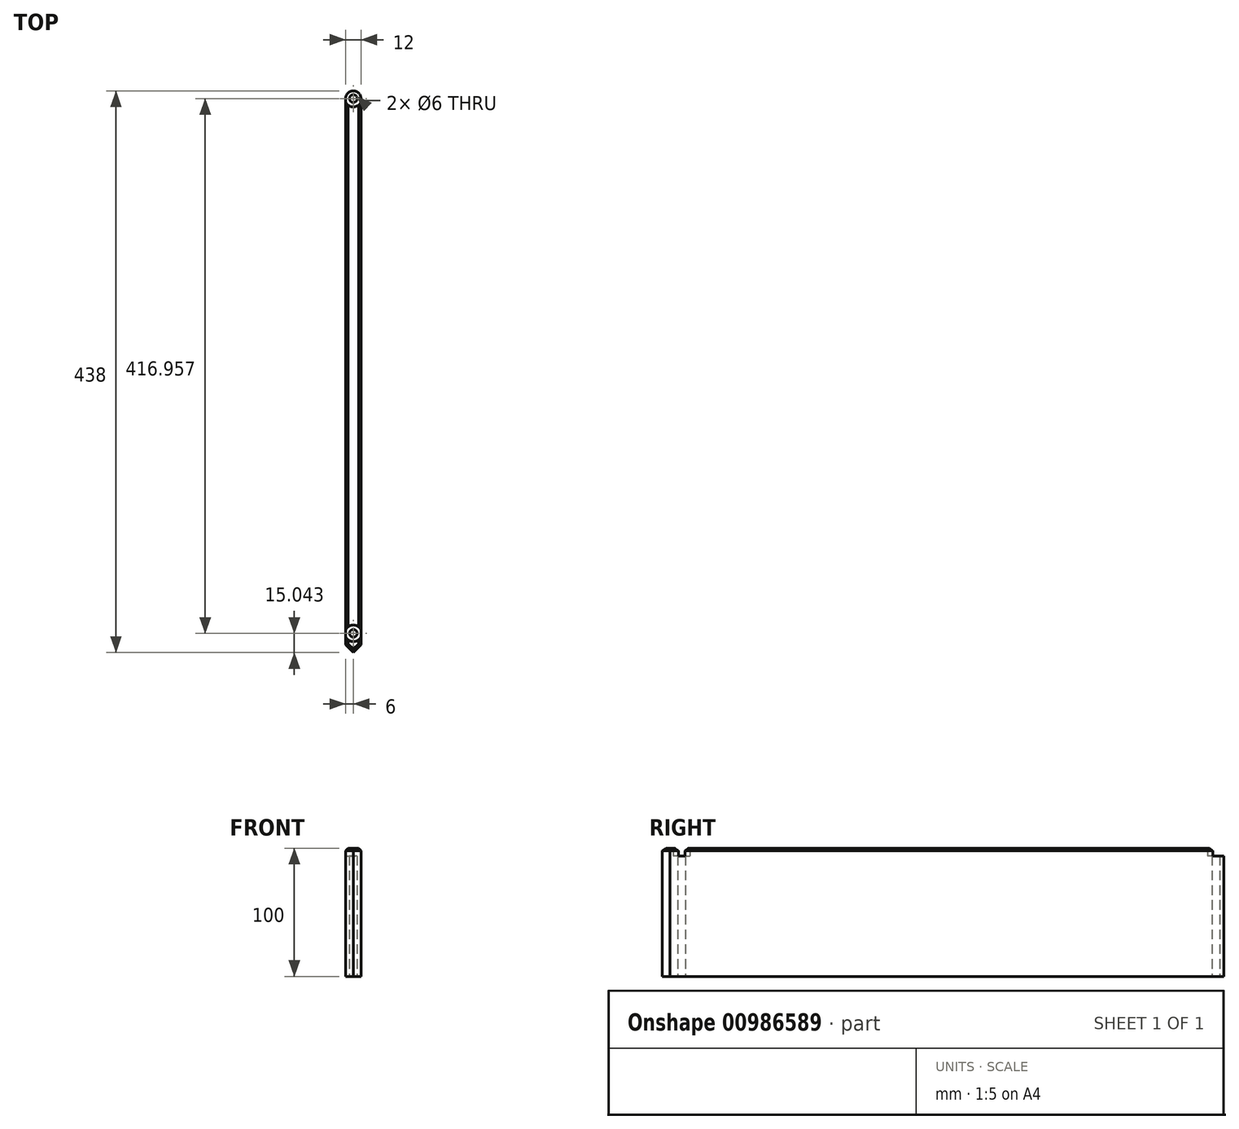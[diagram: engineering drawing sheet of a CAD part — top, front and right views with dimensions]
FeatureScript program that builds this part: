
annotation { "Feature Type Name" : "Feature", "Feature Type Description" : "" }
export const myFeature = defineFeature(function(context is Context, id is Id, definition is map)
    precondition{}
    {
        {
            var Q0;
            Q0=qCreatedBy(makeId("Right.planeOp"),FACE);
            var sketch = newSketch(context, id + "F0", { "sketchPlane" : qUnion([Q0])});
            skLineSegment(sketch, "E0.bottom", {"start": v(0, 0) * mm, "end": v(-438, 0) * mm});
            skLineSegment(sketch, "E0.top", {"start": v(0, 100) * mm, "end": v(-438, 100) * mm});
            skLineSegment(sketch, "E0.left", {"start": v(0, 0) * mm, "end": v(0, 100) * mm});
            skLineSegment(sketch, "E0.right", {"start": v(-438, 0) * mm, "end": v(-438, 100) * mm});
            skSolve(sketch);
        }
        {
            var Q0;
            Q0 = qSketchRegion(id + "F0", true);
            extrude(context, id + "F1", {"entities" : qUnion([Q0]), "depth" : 12 * mm, "offsetDistance" : 25 * mm});
        }
        {
            var Q0;
            Q0=qCreatedBy(makeId("Top.planeOp"),FACE);
            var sketch = newSketch(context, id + "F2", { "sketchPlane" : qUnion([Q0])});
            skCircle(sketch, "E1", {"center": v(6, -6) * mm, "radius": 3 * mm});
            skCircle(sketch, "E2", {"center": v(6, -6) * mm, "radius": 6.5 * mm});
            skCircle(sketch, "E3", {"center": v(6, -422.96) * mm, "radius": 3 * mm});
            skCircle(sketch, "E4", {"center": v(6, -422.96) * mm, "radius": 6.5 * mm});
            skSolve(sketch);
        }
        {
            var Q0;
            Q0=makeQuery(id+"F2.imprint","IMPRINT",FACE,{"disambiguationData":[TD([[makeQuery(id+"F2.imprint","IMPRINT",EDGE,{"derivedFrom":sQuery(id+"F2.wireOp",EDGE,"E3")}),1.0]])]});
            var Q1;
            Q1=makeQuery(id+"F2.imprint","IMPRINT",FACE,{"disambiguationData":[TD([[makeQuery(id+"F2.imprint","IMPRINT",EDGE,{"derivedFrom":sQuery(id+"F2.wireOp",EDGE,"E1")}),1.0]])]});
            extrude(context, id + "F3", {"entities" : qUnion([Q0, Q1]), "operationType" : NewBodyOperationType.REMOVE, "depth" : 120 * mm, "offsetDistance" : 25 * mm});
        }
        {
            var Q0;
            Q0 = qSketchRegion(id + "F2", true);
            extrude(context, id + "F4", {"entities" : qUnion([Q0]), "operationType" : NewBodyOperationType.REMOVE, "depth" : 100 * mm, "offsetDistance" : 25 * mm, "hasSecondDirection" : true, "secondDirectionOppositeDirection" : false, "secondDirectionDepth" : 94 * mm});
        }
        {
            var Q0;
            Q0=makeQuery(id+"F1.opExtrude","CAP_EDGE",EDGE,{"disambiguationData":[OSD([sQuery(id+"F0.wireOp",EDGE,"E0.right")])],"isStart":false});
            var Q1;
            Q1=makeQuery(id+"F1.opExtrude","CAP_EDGE",EDGE,{"disambiguationData":[OSD([sQuery(id+"F0.wireOp",EDGE,"E0.right")])],"isStart":true});
            chamfer(context, id + "F5", {"entities" : qUnion([Q0, Q1]), "width" : 6 * mm, "tangentPropagation" : true});
        }
        {
            var Q0;
            {var subQ0=sQuery(id+"F0.wireOp",EDGE,"E0.right");var subQ1=sQuery(id+"F0.wireOp",EDGE,"E0.top");Q0=makeQuery(id+"F4.boolean.opBoolean","SPLIT",EDGE,{"disambiguationData":[TD([makeQuery(id+"F1.opExtrude","CAP_FACE",FACE,{"disambiguationData":[OSD([sQuery(id+"F0.wireOp",EDGE,"E0.bottom"),subQ1,sQuery(id+"F0.wireOp",EDGE,"E0.left"),subQ0])],"isStart":false}),makeQuery(id+"F1.opExtrude","SWEPT_FACE",FACE,{"disambiguationData":[OSD([subQ1])]}),makeQuery(id+"F1.opExtrude","SWEPT_FACE",FACE,{"disambiguationData":[OSD([subQ0])]}),makeQuery(id+"F4.opExtrude","SWEPT_FACE",FACE,{"disambiguationData":[OSD([sQuery(id+"F2.wireOp",EDGE,"E4")])]})])],"derivedFrom":makeQuery(id+"F1.opExtrude","CAP_EDGE",EDGE,{"disambiguationData":[OSD([subQ1])],"isStart":false})});}
            var Q1;
            {var subQ0=sQuery(id+"F0.wireOp",EDGE,"E0.right");var subQ1=sQuery(id+"F0.wireOp",EDGE,"E0.top");Q1=makeQuery(id+"F4.boolean.opBoolean","SPLIT",EDGE,{"disambiguationData":[TD([makeQuery(id+"F1.opExtrude","CAP_FACE",FACE,{"disambiguationData":[OSD([sQuery(id+"F0.wireOp",EDGE,"E0.bottom"),subQ1,sQuery(id+"F0.wireOp",EDGE,"E0.left"),subQ0])],"isStart":true}),makeQuery(id+"F1.opExtrude","SWEPT_FACE",FACE,{"disambiguationData":[OSD([subQ1])]}),makeQuery(id+"F1.opExtrude","SWEPT_FACE",FACE,{"disambiguationData":[OSD([subQ0])]}),makeQuery(id+"F4.opExtrude","SWEPT_FACE",FACE,{"disambiguationData":[OSD([sQuery(id+"F2.wireOp",EDGE,"E4")])]})])],"derivedFrom":makeQuery(id+"F1.opExtrude","CAP_EDGE",EDGE,{"disambiguationData":[OSD([subQ1])],"isStart":true})});}
            var Q2;
            {var subQ0=sQuery(id+"F0.wireOp",EDGE,"E0.top");Q2=makeQuery(id+"F4.boolean.opBoolean","SPLIT",EDGE,{"disambiguationData":[TD([makeQuery(id+"F1.opExtrude","CAP_FACE",FACE,{"disambiguationData":[OSD([sQuery(id+"F0.wireOp",EDGE,"E0.bottom"),subQ0,sQuery(id+"F0.wireOp",EDGE,"E0.left"),sQuery(id+"F0.wireOp",EDGE,"E0.right")])],"isStart":false}),makeQuery(id+"F1.opExtrude","SWEPT_FACE",FACE,{"disambiguationData":[OSD([subQ0])]}),makeQuery(id+"F4.opExtrude","SWEPT_FACE",FACE,{"disambiguationData":[OSD([sQuery(id+"F2.wireOp",EDGE,"E2")])]}),makeQuery(id+"F4.opExtrude","SWEPT_FACE",FACE,{"disambiguationData":[OSD([sQuery(id+"F2.wireOp",EDGE,"E4")])]})])],"derivedFrom":makeQuery(id+"F1.opExtrude","CAP_EDGE",EDGE,{"disambiguationData":[OSD([subQ0])],"isStart":false})});}
            var Q3;
            {var subQ0=sQuery(id+"F0.wireOp",EDGE,"E0.top");Q3=makeQuery(id+"F4.boolean.opBoolean","SPLIT",EDGE,{"disambiguationData":[TD([makeQuery(id+"F1.opExtrude","CAP_FACE",FACE,{"disambiguationData":[OSD([sQuery(id+"F0.wireOp",EDGE,"E0.bottom"),subQ0,sQuery(id+"F0.wireOp",EDGE,"E0.left"),sQuery(id+"F0.wireOp",EDGE,"E0.right")])],"isStart":true}),makeQuery(id+"F1.opExtrude","SWEPT_FACE",FACE,{"disambiguationData":[OSD([subQ0])]}),makeQuery(id+"F4.opExtrude","SWEPT_FACE",FACE,{"disambiguationData":[OSD([sQuery(id+"F2.wireOp",EDGE,"E2")])]}),makeQuery(id+"F4.opExtrude","SWEPT_FACE",FACE,{"disambiguationData":[OSD([sQuery(id+"F2.wireOp",EDGE,"E4")])]})])],"derivedFrom":makeQuery(id+"F1.opExtrude","CAP_EDGE",EDGE,{"disambiguationData":[OSD([subQ0])],"isStart":true})});}
            var Q4;
            {var subQ0=sQuery(id+"F0.wireOp",EDGE,"E0.right");var subQ1=sQuery(id+"F0.wireOp",EDGE,"E0.left");var subQ2=sQuery(id+"F0.wireOp",EDGE,"E0.top");var subQ3=sQuery(id+"F0.wireOp",EDGE,"E0.bottom");Q4=makeQuery(id+"F5.opChamfer","BLEND_EDGE",EDGE,{"blendedFrom":[makeQuery(id+"F1.opExtrude","CAP_EDGE",EDGE,{"disambiguationData":[OSD([subQ0])],"isStart":false}),makeQuery(id+"F4.boolean.opBoolean","SPLIT",FACE,{"disambiguationData":[TD([makeQuery(id+"F1.opExtrude","CAP_FACE",FACE,{"disambiguationData":[OSD([subQ3,subQ2,subQ1,subQ0])],"isStart":true}),makeQuery(id+"F1.opExtrude","CAP_FACE",FACE,{"disambiguationData":[OSD([subQ3,subQ2,subQ1,subQ0])],"isStart":false}),makeQuery(id+"F1.opExtrude","SWEPT_FACE",FACE,{"disambiguationData":[OSD([subQ0])]}),makeQuery(id+"F4.opExtrude","SWEPT_FACE",FACE,{"disambiguationData":[OSD([sQuery(id+"F2.wireOp",EDGE,"E4")])]})])],"derivedFrom":makeQuery(id+"F1.opExtrude","SWEPT_FACE",FACE,{"disambiguationData":[OSD([subQ2])]})})],"blendedInto":[makeQuery(id+"F4.boolean.opBoolean","SPLIT",FACE,{"disambiguationData":[TD([makeQuery(id+"F1.opExtrude","CAP_FACE",FACE,{"disambiguationData":[OSD([subQ3,subQ2,subQ1,subQ0])],"isStart":true}),makeQuery(id+"F1.opExtrude","CAP_FACE",FACE,{"disambiguationData":[OSD([subQ3,subQ2,subQ1,subQ0])],"isStart":false}),makeQuery(id+"F1.opExtrude","SWEPT_FACE",FACE,{"disambiguationData":[OSD([subQ0])]}),makeQuery(id+"F4.opExtrude","SWEPT_FACE",FACE,{"disambiguationData":[OSD([sQuery(id+"F2.wireOp",EDGE,"E4")])]})])],"derivedFrom":makeQuery(id+"F1.opExtrude","SWEPT_FACE",FACE,{"disambiguationData":[OSD([subQ2])]})})]});}
            var Q5;
            {var subQ0=sQuery(id+"F0.wireOp",EDGE,"E0.right");var subQ1=sQuery(id+"F0.wireOp",EDGE,"E0.left");var subQ2=sQuery(id+"F0.wireOp",EDGE,"E0.top");var subQ3=sQuery(id+"F0.wireOp",EDGE,"E0.bottom");Q5=makeQuery(id+"F5.opChamfer","BLEND_EDGE",EDGE,{"blendedFrom":[makeQuery(id+"F1.opExtrude","CAP_EDGE",EDGE,{"disambiguationData":[OSD([subQ0])],"isStart":true}),makeQuery(id+"F4.boolean.opBoolean","SPLIT",FACE,{"disambiguationData":[TD([makeQuery(id+"F1.opExtrude","CAP_FACE",FACE,{"disambiguationData":[OSD([subQ3,subQ2,subQ1,subQ0])],"isStart":true}),makeQuery(id+"F1.opExtrude","CAP_FACE",FACE,{"disambiguationData":[OSD([subQ3,subQ2,subQ1,subQ0])],"isStart":false}),makeQuery(id+"F1.opExtrude","SWEPT_FACE",FACE,{"disambiguationData":[OSD([subQ0])]}),makeQuery(id+"F4.opExtrude","SWEPT_FACE",FACE,{"disambiguationData":[OSD([sQuery(id+"F2.wireOp",EDGE,"E4")])]})])],"derivedFrom":makeQuery(id+"F1.opExtrude","SWEPT_FACE",FACE,{"disambiguationData":[OSD([subQ2])]})})],"blendedInto":[makeQuery(id+"F4.boolean.opBoolean","SPLIT",FACE,{"disambiguationData":[TD([makeQuery(id+"F1.opExtrude","CAP_FACE",FACE,{"disambiguationData":[OSD([subQ3,subQ2,subQ1,subQ0])],"isStart":true}),makeQuery(id+"F1.opExtrude","CAP_FACE",FACE,{"disambiguationData":[OSD([subQ3,subQ2,subQ1,subQ0])],"isStart":false}),makeQuery(id+"F1.opExtrude","SWEPT_FACE",FACE,{"disambiguationData":[OSD([subQ0])]}),makeQuery(id+"F4.opExtrude","SWEPT_FACE",FACE,{"disambiguationData":[OSD([sQuery(id+"F2.wireOp",EDGE,"E4")])]})])],"derivedFrom":makeQuery(id+"F1.opExtrude","SWEPT_FACE",FACE,{"disambiguationData":[OSD([subQ2])]})})]});}
            chamfer(context, id + "F6", {"entities" : qUnion([Q0, Q1, Q2, Q3, Q4, Q5]), "width" : 2 * mm, "tangentPropagation" : true});
        }
        {
            var Q0;
            Q0=makeQuery(id+"F1.opExtrude","CAP_EDGE",EDGE,{"disambiguationData":[OSD([sQuery(id+"F0.wireOp",EDGE,"E0.left")])],"isStart":false});
            var Q1;
            Q1=makeQuery(id+"F1.opExtrude","CAP_EDGE",EDGE,{"disambiguationData":[OSD([sQuery(id+"F0.wireOp",EDGE,"E0.left")])],"isStart":true});
            fillet(context, id + "F7", {"entities" : qUnion([Q0, Q1]), "radius" : 6 * mm, "tangentPropagation" : true, "allowEdgeOverflow" : false});
        }
    });
